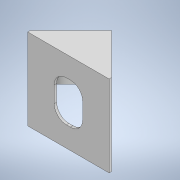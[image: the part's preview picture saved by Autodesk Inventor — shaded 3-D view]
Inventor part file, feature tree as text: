
AUTODESK INVENTOR PART (.ipt)
format: ipt  version: 2020 (Build 240168000, 168)  size: 136,192 bytes
history: native  units: mm
features: extrude x4, sketch x4
ambient origin geometry x8: Origin, YZ Plane, XZ Plane, XY Plane, X Axis, Y Axis, Z Axis, Center Point
bodies: Solid1 (feature_tree)
feature tree (8):
  extrude  "Extrusion1"  Depth=100.0mm
  extrude  "Extrusion2"  TaperAngle=45.0deg  [1 undecoded]
  extrude  "Extrusion3"  Depth=3.0mm
  extrude  "Extrusion4"  Depth=35.0mm
  sketch  "Sketch1"  dims[d0=100.0mm d1=100.0mm]
  sketch  "Sketch2"  dims[d2=3.0mm d3=0.0mm d4=45.0deg]
  sketch  "Sketch3"  dims[d5=3.0mm d6=3.0mm]
  sketch  "Sketch4"  dims[d7=55.0mm d8=0.0mm d9=35.0mm d10=50.0mm d11=15.0mm d12=3.0mm d13=0.0mm d14=3.0mm d15=0.0mm]
note: 1 required parameter value undecoded (feature->parameter linkage not recoverable at this tier; creation-order binding heuristic only, values carry confidence <= 0.55)
